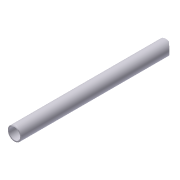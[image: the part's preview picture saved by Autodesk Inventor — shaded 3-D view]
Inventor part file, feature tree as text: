
AUTODESK INVENTOR PART (.ipt)
format: ipt  version: 2012 (Build 160160000, 160)  size: 94,208 bytes
history: native  units: in
note: dims shown in document units (in); Inventor stores cm internally (conversion verified against a paired STEP export)
features: extrude x3, sketch x3, plane x1, other x1, projected_geometry x1
ambient origin geometry x8: Origin, YZ Plane, XZ Plane, XY Plane, X Axis, Y Axis, Z Axis, Center Point
bodies: Solid1 (feature_tree)
feature tree (9):
  extrude  "Extrusion1"  Depth=1.656in
  plane  "Work Plane1"
  extrude  "Extrusion2"  TaperAngle=0.0deg  [1 undecoded]
  extrude  "Extrusion3"  Depth=18.906in
  sketch  "Sketch1"  dims[d0=1.375in d1=1.656in]
  other  "Work Axis1"
  sketch  "Sketch2"  dims[d2=18.469in d3=0.0in d4=0.0in]
  sketch  "Sketch3"  dims[d5=1.6875in d6=18.906in d7=42.0in d8=0.0in d9=0.25in d10=42.0in d11=0.0in]
  projected_geometry  "Projected Loop1"
note: 1 required parameter value undecoded (feature->parameter linkage not recoverable at this tier; creation-order binding heuristic only, values carry confidence <= 0.55)
